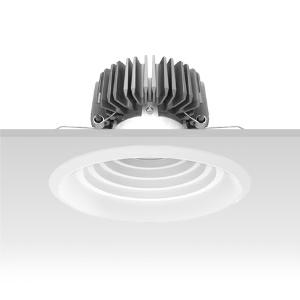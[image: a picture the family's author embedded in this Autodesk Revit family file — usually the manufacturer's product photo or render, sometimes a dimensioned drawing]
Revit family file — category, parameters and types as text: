
# Revit family: 3f_filippi_-_3f_reno_bianco_ugr_3f_filippi_-_30726_-_3f_reno_200_wh_3000-840_ugr
name_source: partatom
category: Lighting Fixtures
units: mm (PartAtom-declared; Revit-internal decimal feet)

## family parameters
Cut with Voids When Loaded = No
Host = Face
Light Source = No
Part Type = Normal
Room Calculation Point = No
Round Connector Dimension = Use Diameter
Shared = No

## types (1)
- 3F Filippi - 3F Reno Bianco UGR (1 x LED, 3300 lm, 28 W, 4000 K)
    Apparent Load = 28 VA
    Approval mark = CE
    CIE Flux Codes = 90 100 100 100 100
    Color Rendering = 80
    Color Temperature = 4000 K
    Control Gear = Electronic ballast
    Default Elevation = 1800 mm
    Description = ILLUMINOTECHNICAL
Luminous efficiency 100% (DLOR 100%, ULOR 0%).
Initial luminous flux of the luminaire 3300 lm.
Direct symmetric UGR distribution.
Installation Interdistance Transv.D = 0.99 x hu - Long.D = 1.01 x hu.
Average luminance <500 cd/m² for radial angles >65°.
Tabular UGR (CIE 117 - 4H-8H; S=0.25H; 70/50/20): RUG 18.4 - 18.3.
Beam angle: 64° - 65°.
Luminous efficacy 118 lm/W.
Lifetime (L90/B10): 30000 h. (tq+25°C)
Lifetime (L85/B10): 50000 h. (tq+25°C)
Lifetime (L70/B10): 80000 h. (tq+25°C)
Sudden decreased luminous flux after 50000 hours: 0% (C0).
Photobiological safety in compliance with IEC/TR 62778: RG1 low risk, (IEC 62471).
In compliance with IEC/EN 62722-2-1 - IEC/EN 62717 standards.

SOURCE
Compact LED module 3000/840.
Energy efficiency class (UE 2019/2020 - UE 2019/2015): D.
CIE 13.3 Colour rendering index: CRI >80 (R9 <50%).
IES TM-30 Fidelity Index: Rf = 84 Rg = 95.
CCT nominal colour temperature 4000 K.
Colour initial tolerance (MacAdam): SDCM 3.
Zhaga Book 3 compliant.

MECHANICAL
Passive heat dissipator in die-casting aluminium, oversized, for optimum thermal management of the LED module.
Parabolic element with graduated/concentric rings in white polycarbonate.
Internal specular metallic louvre to optimise control of the luminous flux in polycarbonate.
Transparent external lens with glossy and satin differentiated surfaces, with a cooling and anti-insect system in methacrylate (PMMA).
Fastening spring clips in stainless steel.
Dimensions: diameter 216 mm, height 142 mm. Weight 1.46 kg.
IP44 protection degree for exposed part, IP20 for recessed part.
Mechanical strength to impacts IK04 (0.5 joule).
Glow-wire test resistance 650°C.

ELECTRICAL
Wiring on a separate unit.
Halogen Free electronic wiring 230V-50/60Hz, power factor 0.95, THD <25%, constant output current, SELV, class II, 1 driver.
Power of the luminaire 28 W.
ENEC - CE.
SAFE FLICKER: PstLM=<1 and SVM=<0.4 (IEC TR 61547-1 and IEC TR 63158), to ensure a more comfortable and safe light.
Luminaire compliant with EN 60598-2-22 for power supply from a centralised emergency system CPSS (Central Power Supply System), not incorporated in the luminaire - high risk areas excluded. The default power and flux are 100% in AC and 100% in DC.
Ambient temperature from 0°C to +25°C.
Temperature class T6 max 85°C.
Relative humidity UR: <85%.

INSTALLATION
Pull-up recessed fitting.
False ceiling carving: 200 mm.
All accessories dedicated to this product are available on the Catalog and on our website www.3F-Filippi.com.

APPLICATIONS
In environments with VDTs, managerial offices and staterooms, public offices and schools.
In false ceilings with narrow voids.

WARNING
Luminaire designed for disposal/recycling at end-of-life.
Replaceable (LED only) light source by a professional. Replaceable control gear by a professional.
    Height = 0 mm  [stored 0 ft]
    Lamp = 1 x LED
    Lamp Light Flux = 3300 lm
    Lamp Power = 28 W
    Lamp count = 1
    Length = 216 mm
    Lifetime = 50000 h
    Luminous efficacy = 118 lm/W
    Manufacturer = 3F Filippi
    ModVariant = No
    Model = 3F Filippi - 30726 - 3F Reno 200 WH 3000-840 UGR
    Mounting Place = Ceiling
    Mounting Type = Recessed
    Number of Poles = 1
    OnlyDefault = Yes
    Power Factor = 1
    Product Name = 3F Filippi - 3F Reno Bianco UGR
    Product group = recessed luminaire
    ProductGroupID = 4
    Protection Class = Protection class II
    Protection Degree = IP 20
    RLX_Detail_Level = 1
    RLX_Emergency_Light_Flux = 0 lm
    RLX_Emergency_Type = 0
    RLX_Emergency_Type_DB = No
    RlxData = <blob elided: 91385 chars, md5=524aa4b7>
    Socket = socket
    Standby Power = 0 W
    System Light Flux = 3300 lm
    System Power = 28 W
    Type Comments = Product without accessories
    Type Image = 3ffilippi_3f_reno_200_wh_2500_3000_4000.jpg
    URL = http://relux.com
    VarID = ---
    Voltage = 0 V
    Weight = 0.00 kg
    Width = 0 mm  [stored 0 ft]

note: [stored X ft] marks values corroborated as IEEE doubles in the binary element streams (Revit-internal decimal feet)

## geometry (parser evidence)
native form markers: Blend x4, Sweep x9
no freeform markers — native parametric forms only
